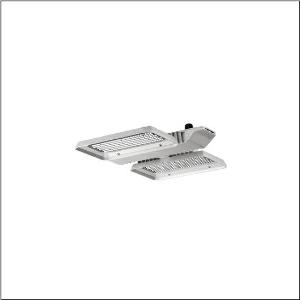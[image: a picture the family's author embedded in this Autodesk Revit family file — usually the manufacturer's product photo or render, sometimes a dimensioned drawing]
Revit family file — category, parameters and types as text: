
# Revit family: highbay_11_51hla2d14fca
name_source: partatom
category: Lighting Fixtures
units: mm (PartAtom-declared; Revit-internal decimal feet)

## family parameters
Cut with Voids When Loaded = No
Host = Face
Light Source = No
Part Type = Normal
Room Calculation Point = No
Round Connector Dimension = Use Diameter
Shared = No

## types (1)
- --- (1 x LED, 14400 lm, 81.2 W, 4000K)
    Apparent Load = 81 VA
    CIE Flux Codes = 89 96 99 100 100
    Color Rendering = 80
    Color Temperature = 4000K
    Default Elevation = 1800 mm
    Description = Highbay 11, LED high bay luminaire, primary light control with lens, of PMMA, light emission: direct distribution, primary light characteristic: symmetric, installation type: surface-mounted, suspended mounting, for 1x 2x LED, rated luminous flux: 14.400lm, luminous efficacy: 177lm/W, light colour: 840, colour temperature: 4000K, control gear: ECG DALI, with terminal, 5-pole, max. 2.5mm², mains connection: 230..240V, AC, 50/60Hz, rated input power: 81W, LED unit, of diecast aluminium, unplated, bead blasted, silver, length: 470mm, width: 500mm, height: 65mm, housing, of diecast aluminium, uncoated, bead blasted, silver, protection rating (complete): IP65, insulation class (complete): insulation class I (protective earthing), certification: CE, ENEC, VDE, UKCA, protection symbol: D, impact resistance: IK08 with glass or PC cover, permissible operating ambient temperature: -35..+55°C, reducing of maximum allowable ambient temperature of 5°C with ceiling mounting, corresponds to IFS (International Featured Standards) requirements for safety and quality in the food industry, packaging unit: 1 piece
    Height = 95 mm
    Lamp = 1 x LED
    Lamp Light Flux = 14400 lm
    Lamp Power = 81.2 W
    Lamp count = 1
    Length = 468 mm
    Luminous efficacy = 177 lm/W
    Manufacturer = Siteco
    ModVariant = No
    Model = 51HLA2D14FCA
    Mounting Place = Ceiling
    Mounting Type = Pendant
    Number of Poles = 1
    OnlyDefault = Yes
    Power Factor = 1
    Product Name = Highbay 11
    Product group = LED high bay luminaire
    ProductGroupID = 903
    Protection Class = Protection class I
    Protection Degree = IP 65
    RLX_Detail_Level = 1
    RLX_Emergency_Light_Flux = 0 lm
    RLX_Emergency_Type = 0
    RLX_Emergency_Type_DB = No
    RlxData = <blob elided: 86149 chars, md5=c0269b40>
    Socket = socket
    Standby Power = 0 W
    System Light Flux = 14400 lm
    System Power = 81 W
    Type Comments = factory setting: luminous flux: 100 % | dim-lin: 254 | 460 mA
    Type Image = l_1003425.jpg
    URL = http://relux.com
    VarID = @adj_160103
    Voltage = 0 V
    Weight = 0.00 kg
    Width = 501 mm

## geometry (parser evidence)
native form markers: Blend x4, Sweep x13
no freeform markers — native parametric forms only
